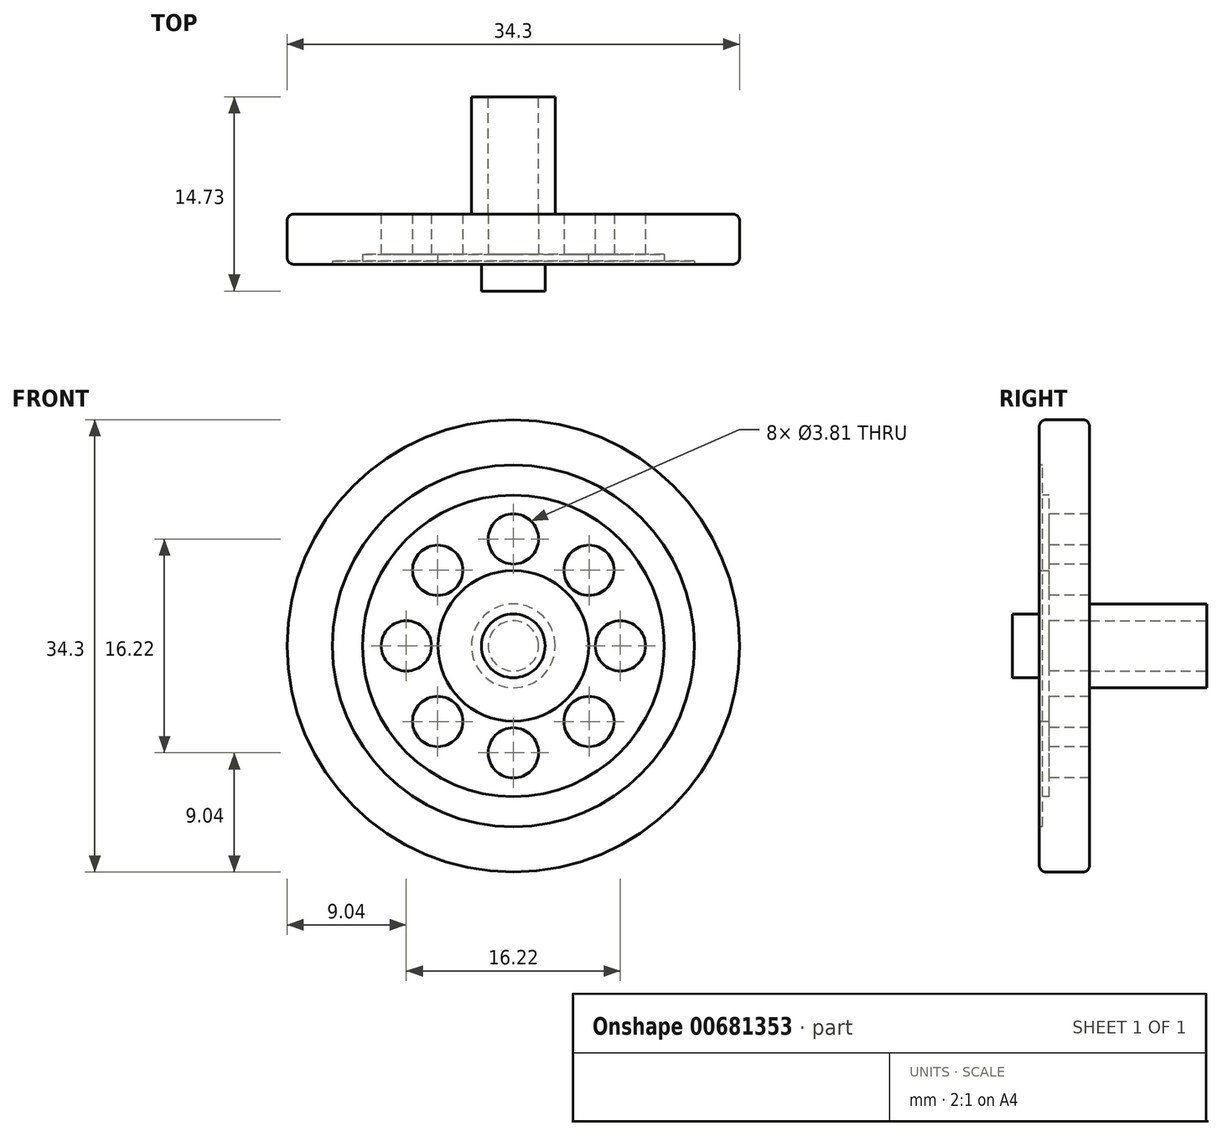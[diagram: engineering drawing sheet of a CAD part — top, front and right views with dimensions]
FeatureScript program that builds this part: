
annotation { "Feature Type Name" : "Feature", "Feature Type Description" : "" }
export const myFeature = defineFeature(function(context is Context, id is Id, definition is map)
    precondition{}
    {
        {
            var Q0;
            Q0=qCreatedBy(makeId("Front.planeOp"),FACE);
            var sketch = newSketch(context, id + "F0", { "sketchPlane" : qUnion([Q0])});
            skCircle(sketch, "E0", {"center": v(0, 0) * mm, "radius": 17.15 * mm});
            skSolve(sketch);
        }
        {
            var Q0;
            Q0=qSketchRegion(id+"F0",true);
            extrude(context, id + "F1", {"entities" : qUnion([Q0]), "depth" : 3.8 * mm, "offsetDistance" : 25.4 * mm});
        }
        {
            var Q0;
            Q0=makeQuery(id+"F1.opExtrude","CAP_FACE",FACE,{"disambiguationData":[OSD([sQuery(id+"F0.wireOp",EDGE,"E0")])],"isStart":false});
            var sketch = newSketch(context, id + "F2", { "sketchPlane" : qUnion([Q0])});
            skCircle(sketch, "E1", {"center": v(0, 0) * mm, "radius": 13.72 * mm});
            skCircle(sketch, "E2", {"center": v(0, 0) * mm, "radius": 11.43 * mm});
            skSolve(sketch);
        }
        {
            var Q0;
            Q0=makeQuery(id+"F2.imprint","IMPRINT",FACE,{"disambiguationData":[TD([[makeQuery(id+"F2.imprint","IMPRINT",EDGE,{"derivedFrom":sQuery(id+"F2.wireOp",EDGE,"E1")}),1.0]])]});
            extrude(context, id + "F3", {"entities" : qUnion([Q0]), "operationType" : NewBodyOperationType.REMOVE, "oppositeDirection" : true, "depth" : 0.25 * mm, "offsetDistance" : 25.4 * mm});
        }
        {
            var Q0;
            Q0=makeQuery(id+"F3.boolean.opBoolean","SPLIT",FACE,{"disambiguationData":[TD([makeQuery(id+"F3.opExtrude","SWEPT_FACE",FACE,{"disambiguationData":[OSD([sQuery(id+"F2.wireOp",EDGE,"E2")])]})])],"derivedFrom":makeQuery(id+"F1.opExtrude","CAP_FACE",FACE,{"disambiguationData":[OSD([sQuery(id+"F0.wireOp",EDGE,"E0")])],"isStart":false})});
            extrude(context, id + "F4", {"entities" : qUnion([Q0]), "operationType" : NewBodyOperationType.REMOVE, "oppositeDirection" : true, "depth" : 0.76 * mm, "offsetDistance" : 25.4 * mm});
        }
        {
            var Q0;
            Q0=makeQuery(id+"F4.boolean.opBoolean","COPY",FACE,{"derivedFrom":makeQuery(id+"F4.opExtrude","CAP_FACE",FACE,{"disambiguationData":[OSD([sQuery(id+"F0.wireOp",EDGE,"E0")])],"isStart":false})});
            var sketch = newSketch(context, id + "F5", { "sketchPlane" : qUnion([Q0])});
            skCircle(sketch, "E3", {"center": v(0, 0) * mm, "radius": 5.71 * mm});
            skSolve(sketch);
        }
        {
            var Q0;
            Q0=makeQuery(id+"F5.imprint","IMPRINT",FACE,{"disambiguationData":[TD([[makeQuery(id+"F5.imprint","IMPRINT",EDGE,{"derivedFrom":sQuery(id+"F5.wireOp",EDGE,"E3")}),1.0]])]});
            extrude(context, id + "F6", {"entities" : qUnion([Q0]), "operationType" : NewBodyOperationType.ADD, "depth" : 0.76 * mm, "offsetDistance" : 25.4 * mm});
        }
        {
            var Q0;
            Q0=makeQuery(id+"F6.opExtrude","CAP_FACE",FACE,{"disambiguationData":[OSD([sQuery(id+"F5.wireOp",EDGE,"E3")])],"isStart":false});
            var sketch = newSketch(context, id + "F7", { "sketchPlane" : qUnion([Q0])});
            skCircle(sketch, "E4", {"center": v(0, 0) * mm, "radius": 2.41 * mm});
            skSolve(sketch);
        }
        {
            var Q0;
            Q0=makeQuery(id+"F4.boolean.opBoolean","COPY",FACE,{"derivedFrom":makeQuery(id+"F4.opExtrude","CAP_FACE",FACE,{"disambiguationData":[OSD([sQuery(id+"F0.wireOp",EDGE,"E0")])],"isStart":false})});
            var sketch = newSketch(context, id + "F8", { "sketchPlane" : qUnion([Q0])});
            skCircle(sketch, "E5", {"center": v(0, 8.11) * mm, "radius": 1.9 * mm});
            skCircle(sketch, "E6.1.0", {"center": v(-5.73, 5.73) * mm, "radius": 1.9 * mm});
            skCircle(sketch, "E6.2.0", {"center": v(-8.11, 0) * mm, "radius": 1.9 * mm});
            skCircle(sketch, "E6.3.0", {"center": v(-5.73, -5.73) * mm, "radius": 1.9 * mm});
            skCircle(sketch, "E6.4.0", {"center": v(0, -8.11) * mm, "radius": 1.9 * mm});
            skCircle(sketch, "E6.5.0", {"center": v(5.73, -5.73) * mm, "radius": 1.9 * mm});
            skCircle(sketch, "E6.6.0", {"center": v(8.11, 0) * mm, "radius": 1.9 * mm});
            skCircle(sketch, "E6.7.0", {"center": v(5.73, 5.73) * mm, "radius": 1.9 * mm});
            skPoint(sketch, "E6.center", {"position": v(0, 0) * mm});
            skSolve(sketch);
        }
        {
            var Q0;
            Q0=makeQuery(id+"F8.imprint","IMPRINT",FACE,{"disambiguationData":[TD([[makeQuery(id+"F8.imprint","IMPRINT",EDGE,{"derivedFrom":sQuery(id+"F8.wireOp",EDGE,"E5")}),1.0]])]});
            var Q1;
            Q1=makeQuery(id+"F8.imprint","IMPRINT",FACE,{"disambiguationData":[TD([[makeQuery(id+"F8.imprint","IMPRINT",EDGE,{"derivedFrom":sQuery(id+"F8.wireOp",EDGE,"E6.1.0")}),1.0]])]});
            var Q2;
            Q2=makeQuery(id+"F8.imprint","IMPRINT",FACE,{"disambiguationData":[TD([[makeQuery(id+"F8.imprint","IMPRINT",EDGE,{"derivedFrom":sQuery(id+"F8.wireOp",EDGE,"E6.3.0")}),1.0]])]});
            var Q3;
            Q3=makeQuery(id+"F8.imprint","IMPRINT",FACE,{"disambiguationData":[TD([[makeQuery(id+"F8.imprint","IMPRINT",EDGE,{"derivedFrom":sQuery(id+"F8.wireOp",EDGE,"E6.4.0")}),1.0]])]});
            var Q4;
            Q4=makeQuery(id+"F8.imprint","IMPRINT",FACE,{"disambiguationData":[TD([[makeQuery(id+"F8.imprint","IMPRINT",EDGE,{"derivedFrom":sQuery(id+"F8.wireOp",EDGE,"E6.5.0")}),1.0]])]});
            var Q5;
            Q5=makeQuery(id+"F8.imprint","IMPRINT",FACE,{"disambiguationData":[TD([[makeQuery(id+"F8.imprint","IMPRINT",EDGE,{"derivedFrom":sQuery(id+"F8.wireOp",EDGE,"E6.6.0")}),1.0]])]});
            var Q6;
            Q6=makeQuery(id+"F8.imprint","IMPRINT",FACE,{"disambiguationData":[TD([[makeQuery(id+"F8.imprint","IMPRINT",EDGE,{"derivedFrom":sQuery(id+"F8.wireOp",EDGE,"E6.7.0")}),1.0]])]});
            var Q7;
            Q7=makeQuery(id+"F8.imprint","IMPRINT",FACE,{"disambiguationData":[TD([[makeQuery(id+"F8.imprint","IMPRINT",EDGE,{"derivedFrom":sQuery(id+"F8.wireOp",EDGE,"E6.2.0")}),1.0]])]});
            extrude(context, id + "F9", {"entities" : qUnion([Q0, Q1, Q2, Q3, Q4, Q5, Q6, Q7]), "operationType" : NewBodyOperationType.REMOVE, "oppositeDirection" : true, "depth" : 25.4 * mm, "offsetDistance" : 25.4 * mm});
        }
        {
            var Q0;
            Q0=makeQuery(id+"F7.imprint","IMPRINT",FACE,{"disambiguationData":[TD([[makeQuery(id+"F7.imprint","IMPRINT",EDGE,{"derivedFrom":sQuery(id+"F7.wireOp",EDGE,"E4")}),1.0]])]});
            var sketch = newSketch(context, id + "F10", { "sketchPlane" : qUnion([Q0])});
            skSolve(sketch);
        }
        {
            var Q0;
            Q0=makeQuery(id+"F10.imprint","IMPRINT",FACE,{"disambiguationData":[TD([[makeQuery(id+"F10.imprint","IMPRINT",EDGE,{"derivedFrom":makeQuery(id+"F7.imprint","IMPRINT",EDGE,{"derivedFrom":sQuery(id+"F7.wireOp",EDGE,"E4")})}),1.0]])]});
            extrude(context, id + "F11", {"entities" : qUnion([Q0]), "operationType" : NewBodyOperationType.ADD, "depth" : 2.03 * mm, "offsetDistance" : 25.4 * mm});
        }
        {
            var Q0;
            Q0=makeQuery(id+"F7.imprint","IMPRINT",FACE,{"disambiguationData":[TD([[makeQuery(id+"F7.imprint","IMPRINT",EDGE,{"derivedFrom":sQuery(id+"F7.wireOp",EDGE,"E4")}),-1.0]])]});
            var sketch = newSketch(context, id + "F12", { "sketchPlane" : qUnion([Q0])});
            skCircle(sketch, "E7", {"center": v(0, 4.32) * mm, "radius": 0.64 * mm});
            skCircle(sketch, "E8.1.0", {"center": v(-2.54, 3.5) * mm, "radius": 0.64 * mm});
            skCircle(sketch, "E8.2.0", {"center": v(-4.11, 1.34) * mm, "radius": 0.64 * mm});
            skCircle(sketch, "E8.3.0", {"center": v(-4.11, -1.34) * mm, "radius": 0.64 * mm});
            skCircle(sketch, "E8.4.0", {"center": v(-2.54, -3.5) * mm, "radius": 0.64 * mm});
            skCircle(sketch, "E8.5.0", {"center": v(0, -4.32) * mm, "radius": 0.64 * mm});
            skCircle(sketch, "E8.6.0", {"center": v(2.54, -3.5) * mm, "radius": 0.64 * mm});
            skCircle(sketch, "E8.7.0", {"center": v(4.11, -1.34) * mm, "radius": 0.64 * mm});
            skCircle(sketch, "E8.8.0", {"center": v(4.11, 1.34) * mm, "radius": 0.64 * mm});
            skCircle(sketch, "E8.9.0", {"center": v(2.54, 3.5) * mm, "radius": 0.64 * mm});
            skPoint(sketch, "E8.center", {"position": v(0, 0) * mm});
            skSolve(sketch);
        }
        {
            var Q0;
            Q0=sQuery(id+"F12.wireOp",EDGE,"E7");
            var Q1;
            Q1=sQuery(id+"F12.wireOp",EDGE,"E8.9.0");
            var Q2;
            Q2=sQuery(id+"F12.wireOp",EDGE,"E8.8.0");
            var Q3;
            Q3=sQuery(id+"F12.wireOp",EDGE,"E8.6.0");
            var Q4;
            Q4=sQuery(id+"F12.wireOp",EDGE,"E8.5.0");
            var Q5;
            Q5=sQuery(id+"F12.wireOp",EDGE,"E8.4.0");
            var Q6;
            Q6=sQuery(id+"F12.wireOp",EDGE,"E8.3.0");
            var Q7;
            Q7=sQuery(id+"F12.wireOp",EDGE,"E8.2.0");
            var Q8;
            Q8=sQuery(id+"F12.wireOp",EDGE,"E8.1.0");
            var Q9;
            Q9=sQuery(id+"F12.wireOp",EDGE,"E8.7.0");
            extrude(context, id + "F13", {"bodyType" : ToolBodyType.SURFACE, "surfaceEntities" : qUnion([Q0, Q1, Q2, Q3, Q4, Q5, Q6, Q7, Q8, Q9]), "depth" : 0.25 * mm, "offsetDistance" : 25.4 * mm});
        }
        {
            var Q0;
            Q0=qCreatedBy(makeId("Front.planeOp"),FACE);
            var sketch = newSketch(context, id + "F14", { "sketchPlane" : qUnion([Q0])});
            skCircle(sketch, "E9", {"center": v(0, 0) * mm, "radius": 3.18 * mm});
            skSolve(sketch);
        }
        {
            var Q0;
            Q0=qSketchRegion(id+"F14",true);
            extrude(context, id + "F15", {"entities" : qUnion([Q0]), "operationType" : NewBodyOperationType.ADD, "oppositeDirection" : true, "depth" : 8.9 * mm, "offsetDistance" : 25.4 * mm});
        }
        {
            var Q0;
            Q0=makeQuery(id+"F15.opExtrude","CAP_FACE",FACE,{"disambiguationData":[OSD([sQuery(id+"F14.wireOp",EDGE,"E9")])],"isStart":false});
            var sketch = newSketch(context, id + "F16", { "sketchPlane" : qUnion([Q0])});
            skCircle(sketch, "E10", {"center": v(0, 0) * mm, "radius": 1.9 * mm});
            skSolve(sketch);
        }
        {
            var Q0;
            Q0=makeQuery(id+"F16.imprint","IMPRINT",FACE,{"disambiguationData":[TD([[makeQuery(id+"F16.imprint","IMPRINT",EDGE,{"derivedFrom":sQuery(id+"F16.wireOp",EDGE,"E10")}),1.0]])]});
            extrude(context, id + "F17", {"entities" : qUnion([Q0]), "operationType" : NewBodyOperationType.REMOVE, "oppositeDirection" : true, "depth" : 8.9 * mm, "offsetDistance" : 25.4 * mm});
        }
        {
            var Q0;
            Q0=makeQuery(id+"F1.opExtrude","CAP_EDGE",EDGE,{"disambiguationData":[OSD([sQuery(id+"F0.wireOp",EDGE,"E0")])],"isStart":false});
            fillet(context, id + "F18", {"entities" : qUnion([Q0]), "radius" : 0.5 * mm, "tangentPropagation" : true, "allowEdgeOverflow" : false});
        }
        {
            var Q0;
            Q0=makeQuery(id+"F1.opExtrude","CAP_EDGE",EDGE,{"disambiguationData":[OSD([sQuery(id+"F0.wireOp",EDGE,"E0")])],"isStart":true});
            fillet(context, id + "F19", {"entities" : qUnion([Q0]), "radius" : 0.5 * mm, "tangentPropagation" : true, "allowEdgeOverflow" : false});
        }
    });
